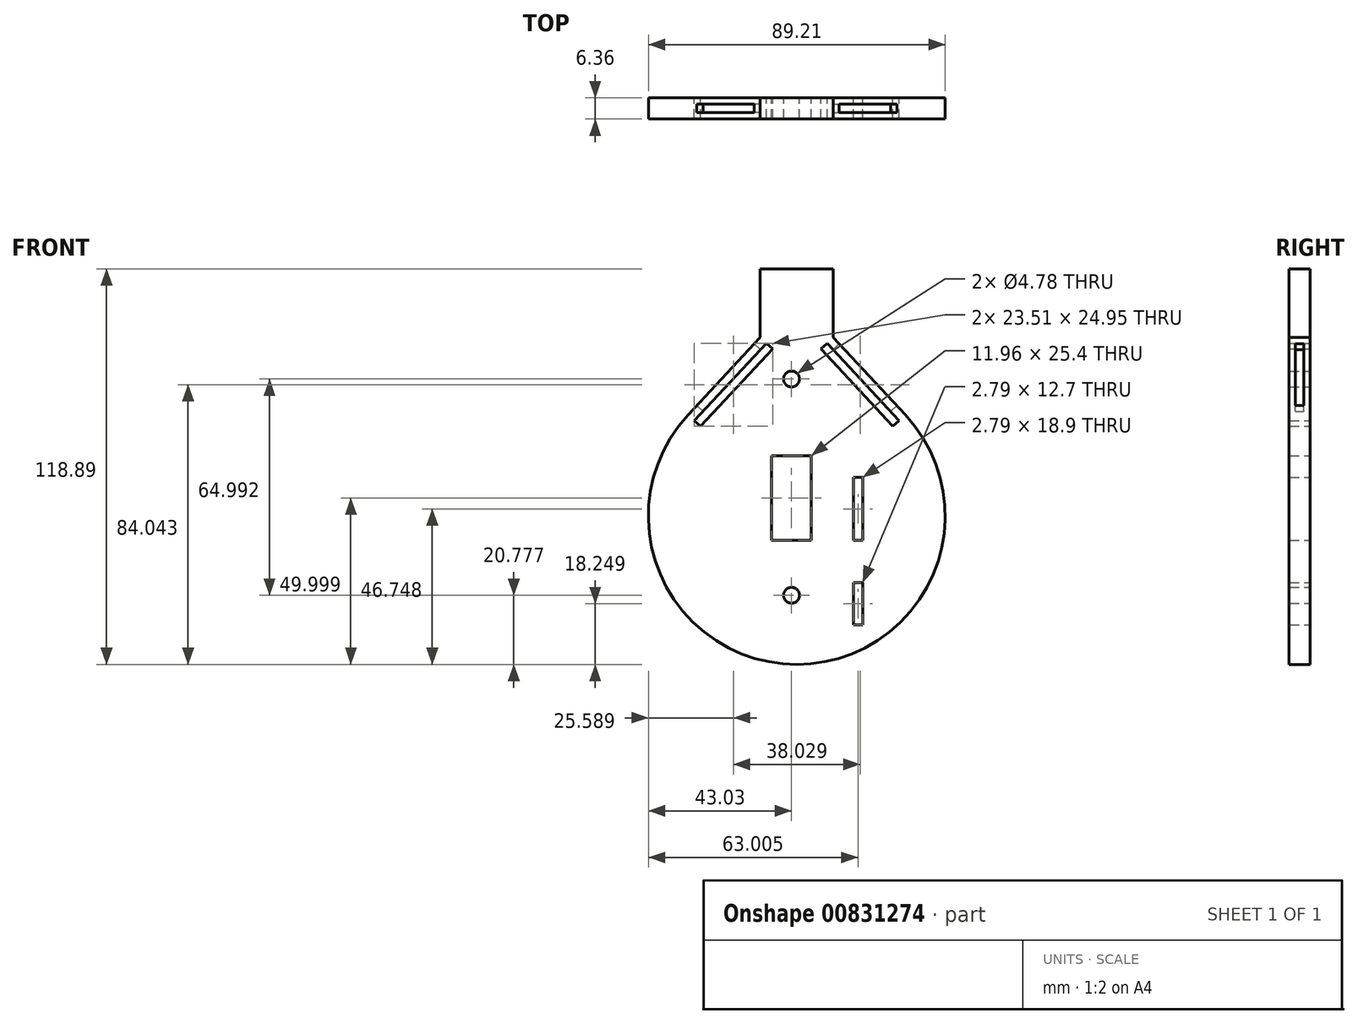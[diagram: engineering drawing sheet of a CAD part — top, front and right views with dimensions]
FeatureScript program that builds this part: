
annotation { "Feature Type Name" : "Feature", "Feature Type Description" : "" }
export const myFeature = defineFeature(function(context is Context, id is Id, definition is map)
    precondition{}
    {
        {
            var Q0;
            Q0=qCreatedBy(makeId("Front.planeOp"),FACE);
            var sketch = newSketch(context, id + "F0", { "sketchPlane" : qUnion([Q0])});
            skArc(sketch, "E0", {"start": v(-31.05, 0) * mm, "mid": v(1.57, -75.03) * mm, "end": v(34.2, 0) * mm});
            skLineSegment(sketch, "E1", {"start": v(-31.05, 0) * mm, "end": v(-9.4, 23.22) * mm});
            skLineSegment(sketch, "E2", {"start": v(34.2, 0) * mm, "end": v(12.55, 23.22) * mm});
            skLineSegment(sketch, "E3", {"start": v(-9.4, 23.22) * mm, "end": v(-9.4, 43.86) * mm});
            skLineSegment(sketch, "E4", {"start": v(12.55, 23.22) * mm, "end": v(12.55, 43.86) * mm});
            skLineSegment(sketch, "E5", {"start": v(-9.4, 43.86) * mm, "end": v(12.55, 43.86) * mm});
            skCircle(sketch, "E6", {"center": v(0, 10.74) * mm, "radius": 2.39 * mm});
            skCircle(sketch, "E7", {"center": v(0, -54.25) * mm, "radius": 2.39 * mm});
            skLineSegment(sketch, "E8.bottom", {"start": v(5.98, -12.33) * mm, "end": v(-5.98, -12.33) * mm});
            skLineSegment(sketch, "E8.top", {"start": v(5.98, -37.73) * mm, "end": v(-5.98, -37.73) * mm});
            skLineSegment(sketch, "E8.left", {"start": v(5.98, -12.33) * mm, "end": v(5.98, -37.73) * mm});
            skLineSegment(sketch, "E8.right", {"start": v(-5.98, -12.33) * mm, "end": v(-5.98, -37.73) * mm});
            skPoint(sketch, "E8.middle", {"position": v(0, -25.03) * mm});
            skLineSegment(sketch, "E9.bottom", {"start": v(18.58, -18.83) * mm, "end": v(21.37, -18.83) * mm});
            skLineSegment(sketch, "E9.top", {"start": v(18.58, -37.73) * mm, "end": v(21.37, -37.73) * mm});
            skLineSegment(sketch, "E9.left", {"start": v(18.58, -18.83) * mm, "end": v(18.58, -37.73) * mm});
            skLineSegment(sketch, "E9.right", {"start": v(21.37, -18.83) * mm, "end": v(21.37, -37.73) * mm});
            skLineSegment(sketch, "E10.bottom", {"start": v(21.37, -50.43) * mm, "end": v(18.58, -50.43) * mm});
            skLineSegment(sketch, "E10.top", {"start": v(21.37, -63.13) * mm, "end": v(18.58, -63.13) * mm});
            skLineSegment(sketch, "E10.left", {"start": v(21.37, -50.43) * mm, "end": v(21.37, -63.13) * mm});
            skLineSegment(sketch, "E10.right", {"start": v(18.58, -50.43) * mm, "end": v(18.58, -63.13) * mm});
            skPoint(sketch, "E10.middle", {"position": v(19.98, -56.78) * mm});
            skLineSegment(sketch, "E11", {"start": v(-7.54, 21.5) * mm, "end": v(-29.2, -1.73) * mm});
            skLineSegment(sketch, "E12", {"start": v(-29.2, -1.73) * mm, "end": v(-27.34, -3.46) * mm});
            skLineSegment(sketch, "E13", {"start": v(-27.34, -3.46) * mm, "end": v(-5.69, 19.76) * mm});
            skLineSegment(sketch, "E14", {"start": v(-5.69, 19.76) * mm, "end": v(-7.54, 21.5) * mm});
            skLineSegment(sketch, "E15", {"start": v(10.7, 21.5) * mm, "end": v(8.83, 19.76) * mm});
            skLineSegment(sketch, "E16", {"start": v(8.83, 19.76) * mm, "end": v(30.49, -3.46) * mm});
            skLineSegment(sketch, "E17", {"start": v(30.49, -3.46) * mm, "end": v(32.34, -1.73) * mm});
            skLineSegment(sketch, "E18", {"start": v(32.34, -1.73) * mm, "end": v(10.7, 21.5) * mm});
            skSolve(sketch);
        }
        {
            var Q0;
            Q0=makeQuery(id+"F0.imprint","IMPRINT",FACE,{"disambiguationData":[TD([[makeQuery(id+"F0.imprint","IMPRINT",EDGE,{"derivedFrom":sQuery(id+"F0.wireOp",EDGE,"E0")}),1.0]])]});
            extrude(context, id + "F1", {"entities" : qUnion([Q0]), "endBound" : BoundingType.SYMMETRIC, "depth" : 6.35 * mm, "offsetDistance" : 25.4 * mm});
        }
        {
            var Q0;
            Q0=makeQuery(id+"F1.opExtrude","SWEPT_FACE",FACE,{"disambiguationData":[OSD([sQuery(id+"F0.wireOp",EDGE,"E1")])]});
            cPlane(context, id + "F2", {"entities" : qUnion([Q0]), "cplaneType" : CPlaneType.OFFSET, "offset" : 0 * mm, "width" : 152.4 * mm, "height" : 152.4 * mm});
        }
        {
            var Q0;
            Q0=qCreatedBy(id+"F2.planeOp",FACE);
            var sketch = newSketch(context, id + "F3", { "sketchPlane" : qUnion([Q0])});
            skLineSegment(sketch, "E19.bottom", {"start": v(-1.27, 7.97) * mm, "end": v(1.27, 7.97) * mm});
            skLineSegment(sketch, "E19.top", {"start": v(-1.27, -17.43) * mm, "end": v(1.27, -17.43) * mm});
            skLineSegment(sketch, "E19.left", {"start": v(-1.27, 7.97) * mm, "end": v(-1.27, -17.43) * mm});
            skLineSegment(sketch, "E19.right", {"start": v(1.27, 7.97) * mm, "end": v(1.27, -17.43) * mm});
            skPoint(sketch, "E19.middle", {"position": v(0, -4.73) * mm});
            skSolve(sketch);
        }
        {
            var Q0;
            Q0=makeQuery(id+"F3.imprint","IMPRINT",FACE,{"disambiguationData":[TD([[makeQuery(id+"F3.imprint","IMPRINT",EDGE,{"derivedFrom":sQuery(id+"F3.wireOp",EDGE,"E19.bottom")}),-1.0]])]});
            extrude(context, id + "F4", {"entities" : qUnion([Q0]), "operationType" : NewBodyOperationType.REMOVE, "oppositeDirection" : true, "depth" : 2.54 * mm, "offsetDistance" : 25.4 * mm});
        }
        {
            var Q0;
            Q0=makeQuery(id+"F1.opExtrude","SWEPT_FACE",FACE,{"disambiguationData":[OSD([sQuery(id+"F0.wireOp",EDGE,"E2")])]});
            cPlane(context, id + "F5", {"entities" : qUnion([Q0]), "cplaneType" : CPlaneType.OFFSET, "offset" : 0 * mm, "width" : 152.4 * mm, "height" : 152.4 * mm});
        }
        {
            var Q0;
            Q0=qCreatedBy(id+"F5.planeOp",FACE);
            var sketch = newSketch(context, id + "F6", { "sketchPlane" : qUnion([Q0])});
            skLineSegment(sketch, "E20.bottom", {"start": v(-1.27, 5.82) * mm, "end": v(1.27, 5.82) * mm});
            skLineSegment(sketch, "E20.top", {"start": v(-1.27, -19.58) * mm, "end": v(1.27, -19.58) * mm});
            skLineSegment(sketch, "E20.left", {"start": v(-1.27, 5.82) * mm, "end": v(-1.27, -19.58) * mm});
            skLineSegment(sketch, "E20.right", {"start": v(1.27, 5.82) * mm, "end": v(1.27, -19.58) * mm});
            skPoint(sketch, "E20.middle", {"position": v(0, -6.88) * mm});
            skSolve(sketch);
        }
        {
            var Q0;
            Q0=makeQuery(id+"F6.imprint","IMPRINT",FACE,{"disambiguationData":[TD([[makeQuery(id+"F6.imprint","IMPRINT",EDGE,{"derivedFrom":sQuery(id+"F6.wireOp",EDGE,"E20.bottom")}),-1.0]])]});
            extrude(context, id + "F7", {"entities" : qUnion([Q0]), "operationType" : NewBodyOperationType.REMOVE, "oppositeDirection" : true, "depth" : 2.54 * mm, "offsetDistance" : 25.4 * mm});
        }
    });
